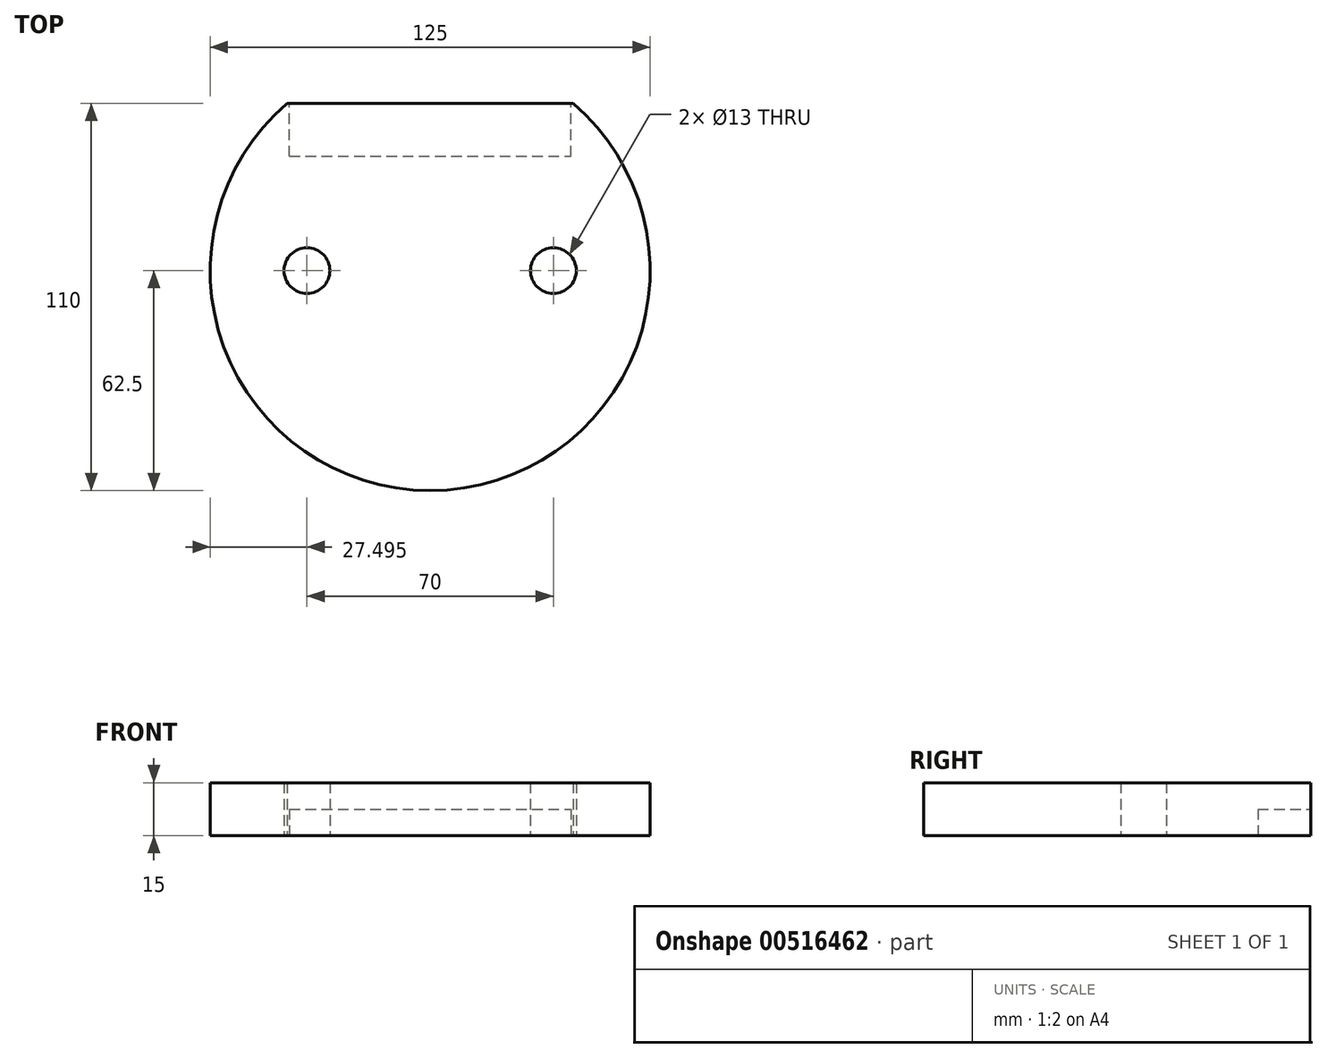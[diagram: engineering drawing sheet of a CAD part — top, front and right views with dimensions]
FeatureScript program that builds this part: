
annotation { "Feature Type Name" : "Feature", "Feature Type Description" : "" }
export const myFeature = defineFeature(function(context is Context, id is Id, definition is map)
    precondition{}
    {
        {
            var Q0;
            Q0=qCreatedBy(makeId("Top.planeOp"),FACE);
            var sketch = newSketch(context, id + "F0", { "sketchPlane" : qUnion([Q0])});
            skLineSegment(sketch, "E0", {"start": v(-75.8, 0) * mm, "end": v(59.2, 0) * mm});
            skLineSegment(sketch, "E1", {"start": v(-8.3, 0) * mm, "end": v(-8.3, -62.5) * mm});
            skLineSegment(sketch, "E2", {"start": v(-8.3, 0) * mm, "end": v(-8.3, 62.5) * mm});
            skCircle(sketch, "E3", {"center": v(-8.3, 0) * mm, "radius": 62.5 * mm});
            skLineSegment(sketch, "E4", {"start": v(-8.3, 0) * mm, "end": v(-43.3, 0) * mm});
            skLineSegment(sketch, "E5", {"start": v(-43.3, 0) * mm, "end": v(-8.3, 0) * mm});
            skLineSegment(sketch, "E6", {"start": v(-8.3, 0) * mm, "end": v(26.7, 0) * mm});
            skCircle(sketch, "E7", {"center": v(-43.3, 0) * mm, "radius": 6.5 * mm});
            skCircle(sketch, "E8", {"center": v(26.7, 0) * mm, "radius": 6.5 * mm});
            skLineSegment(sketch, "E9", {"start": v(-8.3, 62.5) * mm, "end": v(-8.3, 47.5) * mm});
            skLineSegment(sketch, "E10", {"start": v(-8.3, 47.5) * mm, "end": v(-48.91, 47.5) * mm});
            skLineSegment(sketch, "E11", {"start": v(-8.3, 47.5) * mm, "end": v(32.33, 47.5) * mm});
            skSolve(sketch);
        }
        {
            var Q0;
            {var subQ0=sQuery(id+"F0.wireOp",EDGE,"E11");Q0=makeQuery(id+"F0.imprint","IMPRINT",FACE,{"disambiguationData":[TD([[makeQuery(id+"F0.imprint","IMPRINT",EDGE,{"derivedFrom":subQ0}),-1.0]])]});}
            var Q1;
            {var subQ1=sQuery(id+"F0.wireOp",EDGE,"E1");Q1=makeQuery(id+"F0.imprint","IMPRINT",FACE,{"disambiguationData":[TD([[makeQuery(id+"F0.imprint","IMPRINT",EDGE,{"derivedFrom":subQ1}),1.0]])]});}
            var Q2;
            {var subQ3=sQuery(id+"F0.wireOp",EDGE,"E1");Q2=makeQuery(id+"F0.imprint","IMPRINT",FACE,{"disambiguationData":[TD([[makeQuery(id+"F0.imprint","IMPRINT",EDGE,{"derivedFrom":subQ3}),-1.0]])]});}
            var Q3;
            {var subQ3=sQuery(id+"F0.wireOp",EDGE,"E10");Q3=makeQuery(id+"F0.imprint","IMPRINT",FACE,{"disambiguationData":[TD([[makeQuery(id+"F0.imprint","IMPRINT",EDGE,{"derivedFrom":subQ3}),1.0]])]});}
            extrude(context, id + "F1", {"entities" : qUnion([Q0, Q1, Q2, Q3]), "depth" : 15 * mm, "offsetDistance" : 25 * mm});
        }
        {
            var Q0;
            Q0=makeQuery(id+"F1.opExtrude","SWEPT_FACE",FACE,{"disambiguationData":[OSD([sQuery(id+"F0.wireOp",EDGE,"E10"),sQuery(id+"F0.wireOp",EDGE,"E11")])]});
            var sketch = newSketch(context, id + "F2", { "sketchPlane" : qUnion([Q0])});
            skLineSegment(sketch, "E12", {"start": v(48.91, 7.5) * mm, "end": v(-32.33, 7.5) * mm});
            skSolve(sketch);
        }
        {
            var Q0;
            {var subQ0=sQuery(id+"F2.wireOp",EDGE,"E12");Q0=makeQuery(id+"F2.imprint","IMPRINT",FACE,{"disambiguationData":[TD([[makeQuery(id+"F2.imprint","IMPRINT",EDGE,{"derivedFrom":subQ0}),1.0]])]});}
            extrude(context, id + "F3", {"entities" : qUnion([Q0]), "operationType" : NewBodyOperationType.REMOVE, "oppositeDirection" : true, "depth" : 15 * mm, "offsetDistance" : 25 * mm});
        }
        {
            var Q0;
            Q0=makeQuery(id+"F3.boolean.opBoolean","COPY",FACE,{"derivedFrom":makeQuery(id+"F3.opExtrude","SWEPT_FACE",FACE,{"disambiguationData":[OSD([sQuery(id+"F0.wireOp",EDGE,"E3"),sQuery(id+"F0.wireOp",EDGE,"E10")])]})});
            extrude(context, id + "F4", {"entities" : qUnion([Q0]), "operationType" : NewBodyOperationType.ADD, "depth" : 0.62 * mm, "offsetDistance" : 25 * mm});
        }
        {
            var Q0;
            Q0=makeQuery(id+"F3.boolean.opBoolean","COPY",FACE,{"derivedFrom":makeQuery(id+"F3.opExtrude","SWEPT_FACE",FACE,{"disambiguationData":[OSD([sQuery(id+"F0.wireOp",EDGE,"E3"),sQuery(id+"F0.wireOp",EDGE,"E11")])]})});
            extrude(context, id + "F5", {"entities" : qUnion([Q0]), "operationType" : NewBodyOperationType.ADD, "depth" : 0.62 * mm, "offsetDistance" : 25 * mm});
        }
    });
